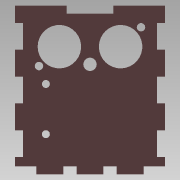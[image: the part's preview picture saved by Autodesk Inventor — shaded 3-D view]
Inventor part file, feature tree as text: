
AUTODESK INVENTOR PART (.ipt)
format: ipt  version: 2015 SP1 (Build 190203100, 203)  size: 155,648 bytes
history: native  units: mm
features: extrude x1, sketch x1
ambient origin geometry x8: Origin, YZ Plane, XZ Plane, XY Plane, X Axis, Y Axis, Z Axis, Center Point
bodies: Body1 (feature_tree)
feature tree (2):
  extrude  "Extrusion2"  Depth=20.0mm
  sketch  "Sketch1"  dims[d2=3.0mm d3=20.0mm d5=15.0mm d6=20.0mm d8=15.0mm d11=10.0mm d12=5.0mm d13=10.0mm d16=3.0mm d17=3.0mm d18=3.0mm d19=0.0mm]
